# Revit family: BDG_BossDesign_Stng_Myriad_90Degree
name_source: partatom
category: Furniture
revit_build: Autodesk Revit 2015 (Build: 20140903_1530(x64)
units: mm (PartAtom-declared; Revit-internal decimal feet)

## types (3) — shared parameters
Assembly Code = E2020200
AssetType = Movable
BIMObjectName = BDG_BossDesign_Seating_Myriad_90Degree
Category = Pr_40_50_12 : Chairs, seats and benches
CodePerformance = BSEN 16139:2013
Color = Various
DurationUnit = year
ExpectedLife = 5
Features = CMHR foam body
Finish = Fully upholstered
IfcExportAs = IfcFurnishingElementType
IfcExportType = CHAIR
Keynote = Pr_40_50_12
MainColor = Various
ManufacturerName = Boss Design
ManufacturerURL = www.bossdesign.com
Material = Fabric and Oak Legs
NBSDescription = Seating
NBSReference = 45-35-72/352
Name = Seating_Myriad_90Degree_BossDesign
NominalLength = 1340 mm  [stored 4.39633 ft]
NominalWidth = 1340 mm  [stored 4.39633 ft]
ProductInformation = www.bossdesign.com/product-list/myriad/
Shape = Square
Size = 1340 x 1340 x 460mm
SustainabilityPerformance = 99% Recyclable
URL = www.bossdesign.com
Uniclass2015Code = Pr_40_50_12
Uniclass2015Title = Chairs, seats and benches
Uniclass2015Version = Products v1.10
Version = 1
WarrantyDescription = Structural Warranty Excludes Foams and Fabrics
WarrantyDurationLabor = 5
WarrantyDurationParts = 5
WarrantyDurationUnit = year

## per-type parameters (varying)
| type | IsMYR90 | IsMYR90ES | IsMYR90IS | Model | ModelNumber | NominalHeight |
| 90 Degree without Back | Yes | No | No | MYR/90 | MYR/90 | 460 mm  [stored 1.50919 ft] |
| 90 Degree with External Seat | No | Yes | No | MYR/90/ES | MYR/90/ES | 788 mm |
| 90 Degree with Internal Seat | No | No | Yes | MYR/90/IS | MYR/90/IS | 788 mm |

note: column(s) folded — value = type name in every type: Description, ModelReference

note: [stored X ft] marks values corroborated as IEEE doubles in the binary element streams (Revit-internal decimal feet)

## geometry (parser evidence)
native form markers: Sweep x6
no freeform markers — native parametric forms only
